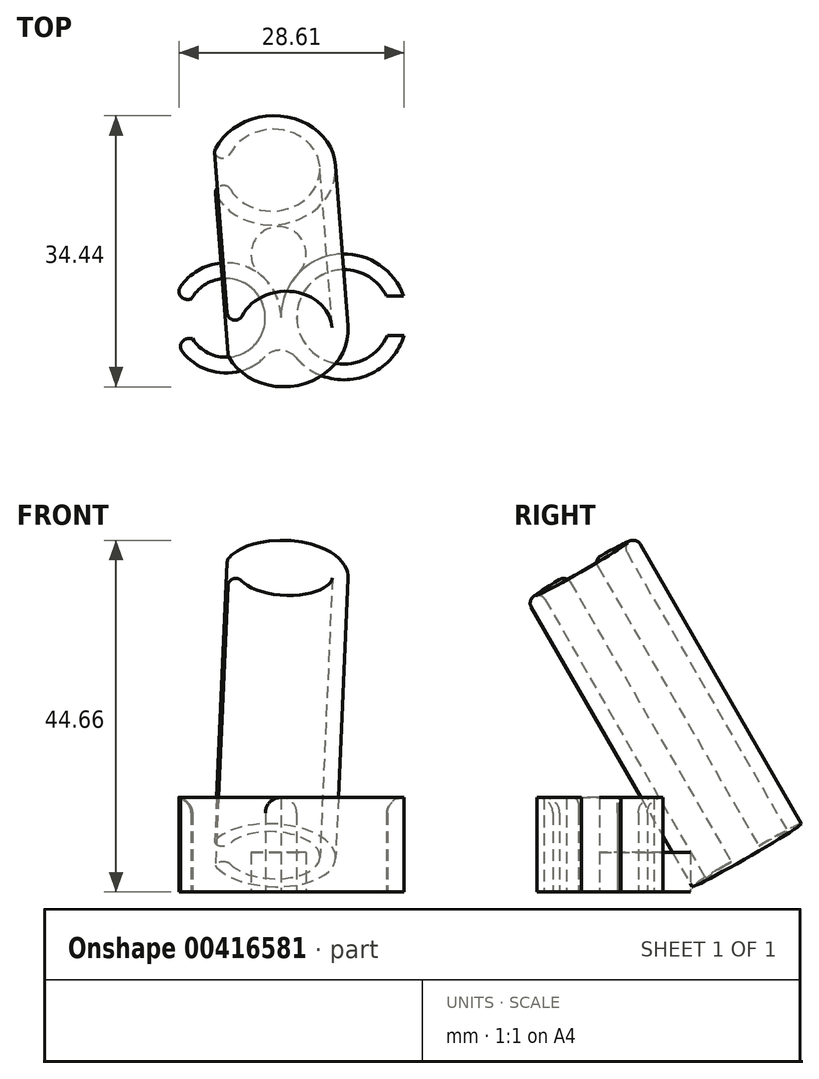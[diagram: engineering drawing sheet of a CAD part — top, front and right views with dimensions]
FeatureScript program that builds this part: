
annotation { "Feature Type Name" : "Feature", "Feature Type Description" : "" }
export const myFeature = defineFeature(function(context is Context, id is Id, definition is map)
    precondition{}
    {
        {
            var Q0;
            Q0=qCreatedBy(makeId("Top.planeOp"),FACE);
            var sketch = newSketch(context, id + "F0", { "sketchPlane" : qUnion([Q0])});
            skArc(sketch, "E0", {"start": v(-58.3, -57.6) * mm, "mid": v(-64.14, -50.76) * mm, "end": v(-71.9, -55.33) * mm});
            skArc(sketch, "E1", {"start": v(-56.4, -62.7) * mm, "mid": v(-48.68, -65.36) * mm, "end": v(-42.65, -59.87) * mm});
            skArc(sketch, "E2", {"start": v(-44.9, -54.91) * mm, "mid": v(-56.3, -57.66) * mm, "end": v(-44.79, -59.9) * mm});
            skArc(sketch, "E3", {"start": v(-69.55, -60.28) * mm, "mid": v(-60.3, -57.52) * mm, "end": v(-69.7, -55.3) * mm});
            skArc(sketch, "E4", {"start": v(-56.4, -62.7) * mm, "mid": v(-58.31, -61.77) * mm, "end": v(-60.3, -62.56) * mm});
            skLineSegment(sketch, "E5", {"start": v(-42.75, -54.88) * mm, "end": v(-44.9, -54.91) * mm});
            skLineSegment(sketch, "E6", {"start": v(-71.77, -60.32) * mm, "end": v(-69.55, -60.28) * mm});
            skArc(sketch, "E7.trimOffspring", {"start": v(-42.75, -54.88) * mm, "mid": v(-51.67, -49.65) * mm, "end": v(-58.3, -57.6) * mm});
            skArc(sketch, "E8.trimOffspring", {"start": v(-71.77, -60.32) * mm, "mid": v(-66.64, -64.53) * mm, "end": v(-60.3, -62.56) * mm});
            skPoint(sketch, "E9.start.orphan", {"position": v(-38.97, -59.82) * mm});
            skPoint(sketch, "E10.orphan", {"position": v(-39.31, -54.83) * mm});
            skLineSegment(sketch, "E11.trimOffspring", {"start": v(-69.7, -55.3) * mm, "end": v(-71.9, -55.33) * mm});
            skLineSegment(sketch, "E12.trimOffspring", {"start": v(-44.79, -59.9) * mm, "end": v(-42.65, -59.87) * mm});
            skSolve(sketch);
        }
        {
            var Q0;
            Q0=qSketchRegion(id+"F0",true);
            extrude(context, id + "F1", {"entities" : qUnion([Q0]), "depth" : 12 * mm});
        }
        {
            var Q0;
            Q0=makeQuery(id+"F1.opExtrude","CAP_FACE",FACE,{"disambiguationData":[OSD([sQuery(id+"F0.wireOp",EDGE,"E0"),sQuery(id+"F0.wireOp",EDGE,"E1"),sQuery(id+"F0.wireOp",EDGE,"E2"),sQuery(id+"F0.wireOp",EDGE,"E3"),sQuery(id+"F0.wireOp",EDGE,"E4"),sQuery(id+"F0.wireOp",EDGE,"E5"),sQuery(id+"F0.wireOp",EDGE,"E6"),sQuery(id+"F0.wireOp",EDGE,"E7.trimOffspring"),sQuery(id+"F0.wireOp",EDGE,"E8.trimOffspring"),sQuery(id+"F0.wireOp",EDGE,"E11.trimOffspring"),sQuery(id+"F0.wireOp",EDGE,"E12.trimOffspring")])],"isStart":false});
            var sketch = newSketch(context, id + "F2", { "sketchPlane" : qUnion([Q0])});
            skCircle(sketch, "E13", {"center": v(-58.95, -44.07) * mm, "radius": 8 * mm});
            skCircle(sketch, "E14", {"center": v(-58.95, -44.07) * mm, "radius": 6 * mm});
            skLineSegment(sketch, "E15", {"start": v(-58.95, -44.07) * mm, "end": v(-57.68, -70.65) * mm, "construction": true});
            skSolve(sketch);
        }
        {
            var Q0;
            Q0=qSketchRegion(id+"F2",true);
            extrude(context, id + "F3", {"entities" : qUnion([Q0]), "oppositeDirection" : true, "depth" : 12 * mm, "offsetDistance" : 25 * mm});
        }
        {
            var Q0;
            Q0=makeQuery(id+"F3.opExtrude","CAP_FACE",FACE,{"disambiguationData":[OSD([sQuery(id+"F2.wireOp",EDGE,"E13"),sQuery(id+"F2.wireOp",EDGE,"E14")])],"isStart":true});
            var sketch = newSketch(context, id + "F4", { "sketchPlane" : qUnion([Q0])});
            skCircle(sketch, "E16.0", {"center": v(-58.95, -44.07) * mm, "radius": 8 * mm});
            skSolve(sketch);
        }
        {
            var Q0;
            Q0=makeQuery(id+"F4.imprint","IMPRINT",FACE,{"disambiguationData":[TD([[makeQuery(id+"F4.imprint","IMPRINT",EDGE,{"derivedFrom":sQuery(id+"F4.wireOp",EDGE,"E16.0")}),1.0]])]});
            var Q1;
            Q1=sQuery(id+"F4.wireOp",EDGE,"E16.0");
            var Q2;
            Q2=sQuery(id+"F2.wireOp",EDGE,"E14");
            extrude(context, id + "F5", {"entities" : qUnion([Q0]), "surfaceEntities" : qUnion([Q1, Q2]), "depth" : 30 * mm, "offsetDistance" : 25 * mm});
        }
        {
            var Q0;
            Q0=makeQuery(id+"F5.opExtrude","SWEPT_BODY",BODY,{"disambiguationData":[OSD([sQuery(id+"F2.wireOp",EDGE,"E14"),sQuery(id+"F4.wireOp",EDGE,"E16.0")])]});
            var Q1;
            Q1=makeQuery(id+"F3.opExtrude","SWEPT_BODY",BODY,{"disambiguationData":[OSD([sQuery(id+"F2.wireOp",EDGE,"E13"),sQuery(id+"F2.wireOp",EDGE,"E14")])]});
            booleanBodies(context, id + "F6", {"operationType" : BooleanOperationType.UNION, "tools" : qUnion([Q0, Q1])});
        }
        {
            var Q0;
            Q0=makeQuery(id+"F5.opExtrude","CAP_FACE",FACE,{"disambiguationData":[OSD([sQuery(id+"F2.wireOp",EDGE,"E14"),sQuery(id+"F4.wireOp",EDGE,"E16.0")])],"isStart":false});
            var sketch = newSketch(context, id + "F7", { "sketchPlane" : qUnion([Q0])});
            skLineSegment(sketch, "E17", {"start": v(-58.95, -44.07) * mm, "end": v(-74.2, -44.07) * mm});
            skLineSegment(sketch, "E18", {"start": v(-69.52, -42.23) * mm, "end": v(-62.49, -42.23) * mm});
            skLineSegment(sketch, "E19", {"start": v(-62.49, -42.23) * mm, "end": v(-62.49, -46.23) * mm});
            skLineSegment(sketch, "E20", {"start": v(-62.49, -46.23) * mm, "end": v(-69.52, -46.23) * mm});
            skLineSegment(sketch, "E21", {"start": v(-69.52, -42.23) * mm, "end": v(-69.52, -46.23) * mm});
            skSolve(sketch);
        }
        {
            var Q0;
            Q0=qSketchRegion(id+"F7",true);
            extrude(context, id + "F8", {"entities" : qUnion([Q0]), "operationType" : NewBodyOperationType.REMOVE, "oppositeDirection" : true, "depth" : 50 * mm, "offsetDistance" : 25 * mm});
        }
        {
            var Q0;
            Q0=makeQuery(id+"F1.opExtrude","CAP_FACE",FACE,{"disambiguationData":[OSD([sQuery(id+"F0.wireOp",EDGE,"E0"),sQuery(id+"F0.wireOp",EDGE,"E1"),sQuery(id+"F0.wireOp",EDGE,"E2"),sQuery(id+"F0.wireOp",EDGE,"E3"),sQuery(id+"F0.wireOp",EDGE,"E4"),sQuery(id+"F0.wireOp",EDGE,"E5"),sQuery(id+"F0.wireOp",EDGE,"E6"),sQuery(id+"F0.wireOp",EDGE,"E7.trimOffspring"),sQuery(id+"F0.wireOp",EDGE,"E8.trimOffspring"),sQuery(id+"F0.wireOp",EDGE,"E11.trimOffspring"),sQuery(id+"F0.wireOp",EDGE,"E12.trimOffspring")])],"isStart":false});
            var sketch = newSketch(context, id + "F9", { "sketchPlane" : qUnion([Q0])});
            skPoint(sketch, "E22.endSnap0", {"position": v(-51.67, -49.65) * mm});
            skLineSegment(sketch, "E23", {"start": v(-65.3, -50.66) * mm, "end": v(-50.91, -49.55) * mm, "construction": true});
            skSolve(sketch);
        }
        {
            var Q0;
            Q0=makeQuery(id+"F5.opExtrude","SWEPT_BODY",BODY,{"disambiguationData":[OSD([sQuery(id+"F2.wireOp",EDGE,"E14"),sQuery(id+"F4.wireOp",EDGE,"E16.0")])]});
            var Q1;
            Q1=sQuery(id+"F9.wireOp",EDGE,"E23");
            transform(context, id + "F10", {"entities" : qUnion([Q0]), "transformType" : TransformType.ROTATION, "transformAxis" : qUnion([Q1]), "angle" : 30 * degree, "makeCopy" : false});
        }
        {
            var Q0;
            Q0=makeQuery(id+"F1.opExtrude","CAP_FACE",FACE,{"disambiguationData":[OSD([sQuery(id+"F0.wireOp",EDGE,"E0"),sQuery(id+"F0.wireOp",EDGE,"E1"),sQuery(id+"F0.wireOp",EDGE,"E2"),sQuery(id+"F0.wireOp",EDGE,"E3"),sQuery(id+"F0.wireOp",EDGE,"E4"),sQuery(id+"F0.wireOp",EDGE,"E5"),sQuery(id+"F0.wireOp",EDGE,"E6"),sQuery(id+"F0.wireOp",EDGE,"E7.trimOffspring"),sQuery(id+"F0.wireOp",EDGE,"E8.trimOffspring"),sQuery(id+"F0.wireOp",EDGE,"E11.trimOffspring"),sQuery(id+"F0.wireOp",EDGE,"E12.trimOffspring")])],"isStart":true});
            var sketch = newSketch(context, id + "F11", { "sketchPlane" : qUnion([Q0])});
            skArc(sketch, "E24", {"start": v(-60.83, 52.27) * mm, "mid": v(-58.8, 46.08) * mm, "end": v(-56.07, 52) * mm});
            skArc(sketch, "E25.0", {"start": v(-56.07, 52) * mm, "mid": v(-57.73, 54.58) * mm, "end": v(-58.3, 57.6) * mm});
            skArc(sketch, "E26.0", {"start": v(-58.3, 57.6) * mm, "mid": v(-58.97, 54.65) * mm, "end": v(-60.83, 52.27) * mm});
            skPoint(sketch, "E27.orphan", {"position": v(-42.75, 54.88) * mm});
            skPoint(sketch, "E28.orphan", {"position": v(-71.9, 55.33) * mm});
            skSolve(sketch);
        }
        {
            var Q0;
            Q0=qSketchRegion(id+"F11",true);
            extrude(context, id + "F12", {"entities" : qUnion([Q0]), "oppositeDirection" : true, "depth" : 5 * mm, "offsetDistance" : 25 * mm});
        }
        {
            var Q0;
            {var subQ0=sQuery(id+"F2.wireOp",EDGE,"E14");Q0=makeQuery(id+"F8.boolean.opBoolean","INTERSECT",EDGE,{"derivedFrom":[makeQuery(id+"F6.opBoolean","MERGE",FACE,{"derivedFrom":[makeQuery(id+"F3.opExtrude","SWEPT_FACE",FACE,{"disambiguationData":[OSD([subQ0])]}),makeQuery(id+"F5.opExtrude","SWEPT_FACE",FACE,{"disambiguationData":[OSD([subQ0])]})]}),makeQuery(id+"F8.opExtrude","SWEPT_FACE",FACE,{"disambiguationData":[OSD([sQuery(id+"F7.wireOp",EDGE,"E18")])]})]});}
            var Q1;
            Q1=makeQuery(id+"F8.boolean.opBoolean","INTERSECT",EDGE,{"derivedFrom":[makeQuery(id+"F6.opBoolean","MERGE",FACE,{"derivedFrom":[makeQuery(id+"F3.opExtrude","SWEPT_FACE",FACE,{"disambiguationData":[OSD([sQuery(id+"F2.wireOp",EDGE,"E13")])]}),makeQuery(id+"F5.opExtrude","SWEPT_FACE",FACE,{"disambiguationData":[OSD([sQuery(id+"F4.wireOp",EDGE,"E16.0")])]})]}),makeQuery(id+"F8.opExtrude","SWEPT_FACE",FACE,{"disambiguationData":[OSD([sQuery(id+"F7.wireOp",EDGE,"E18")])]})]});
            fillet(context, id + "F13", {"entities" : qUnion([Q0, Q1]), "radius" : 1 * mm, "tangentPropagation" : true, "allowEdgeOverflow" : false});
        }
        {
            var Q0;
            {var subQ0=sQuery(id+"F2.wireOp",EDGE,"E14");Q0=makeQuery(id+"F8.boolean.opBoolean","INTERSECT",EDGE,{"derivedFrom":[makeQuery(id+"F6.opBoolean","MERGE",FACE,{"derivedFrom":[makeQuery(id+"F3.opExtrude","SWEPT_FACE",FACE,{"disambiguationData":[OSD([subQ0])]}),makeQuery(id+"F5.opExtrude","SWEPT_FACE",FACE,{"disambiguationData":[OSD([subQ0])]})]}),makeQuery(id+"F8.opExtrude","SWEPT_FACE",FACE,{"disambiguationData":[OSD([sQuery(id+"F7.wireOp",EDGE,"E20")])]})]});}
            var Q1;
            Q1=makeQuery(id+"F8.boolean.opBoolean","INTERSECT",EDGE,{"derivedFrom":[makeQuery(id+"F6.opBoolean","MERGE",FACE,{"derivedFrom":[makeQuery(id+"F3.opExtrude","SWEPT_FACE",FACE,{"disambiguationData":[OSD([sQuery(id+"F2.wireOp",EDGE,"E13")])]}),makeQuery(id+"F5.opExtrude","SWEPT_FACE",FACE,{"disambiguationData":[OSD([sQuery(id+"F4.wireOp",EDGE,"E16.0")])]})]}),makeQuery(id+"F8.opExtrude","SWEPT_FACE",FACE,{"disambiguationData":[OSD([sQuery(id+"F7.wireOp",EDGE,"E20")])]})]});
            fillet(context, id + "F14", {"entities" : qUnion([Q0, Q1]), "radius" : 1 * mm, "tangentPropagation" : true, "allowEdgeOverflow" : false});
        }
        {
            var Q0;
            Q0=makeQuery(id+"F5.opExtrude","CAP_EDGE",EDGE,{"disambiguationData":[OSD([sQuery(id+"F2.wireOp",EDGE,"E14")])],"isStart":false});
            fillet(context, id + "F15", {"entities" : qUnion([Q0]), "radius" : 1 * mm, "tangentPropagation" : true, "allowEdgeOverflow" : false});
        }
        {
            var Q0;
            Q0=makeQuery(id+"F1.opExtrude","CAP_EDGE",EDGE,{"disambiguationData":[OSD([sQuery(id+"F0.wireOp",EDGE,"E3")])],"isStart":false});
            fillet(context, id + "F16", {"entities" : qUnion([Q0]), "radius" : 2 * mm, "tangentPropagation" : true, "allowEdgeOverflow" : false});
        }
        {
            var Q0;
            Q0=makeQuery(id+"F1.opExtrude","CAP_EDGE",EDGE,{"disambiguationData":[OSD([sQuery(id+"F0.wireOp",EDGE,"E2")])],"isStart":false});
            fillet(context, id + "F17", {"entities" : qUnion([Q0]), "radius" : 2 * mm, "tangentPropagation" : true, "allowEdgeOverflow" : false});
        }
        {
            var Q0;
            Q0=makeQuery(id+"F1.opExtrude","SWEPT_EDGE",EDGE,{"disambiguationData":[OSD([sQuery(id+"F0.wireOp",EDGE,"E0"),sQuery(id+"F0.wireOp",EDGE,"E11.trimOffspring")])]});
            var Q1;
            Q1=makeQuery(id+"F1.opExtrude","SWEPT_EDGE",EDGE,{"disambiguationData":[OSD([sQuery(id+"F0.wireOp",EDGE,"E6"),sQuery(id+"F0.wireOp",EDGE,"E8.trimOffspring")])]});
            fillet(context, id + "F18", {"entities" : qUnion([Q0, Q1]), "radius" : 1 * mm, "tangentPropagation" : true, "allowEdgeOverflow" : false});
        }
    });
